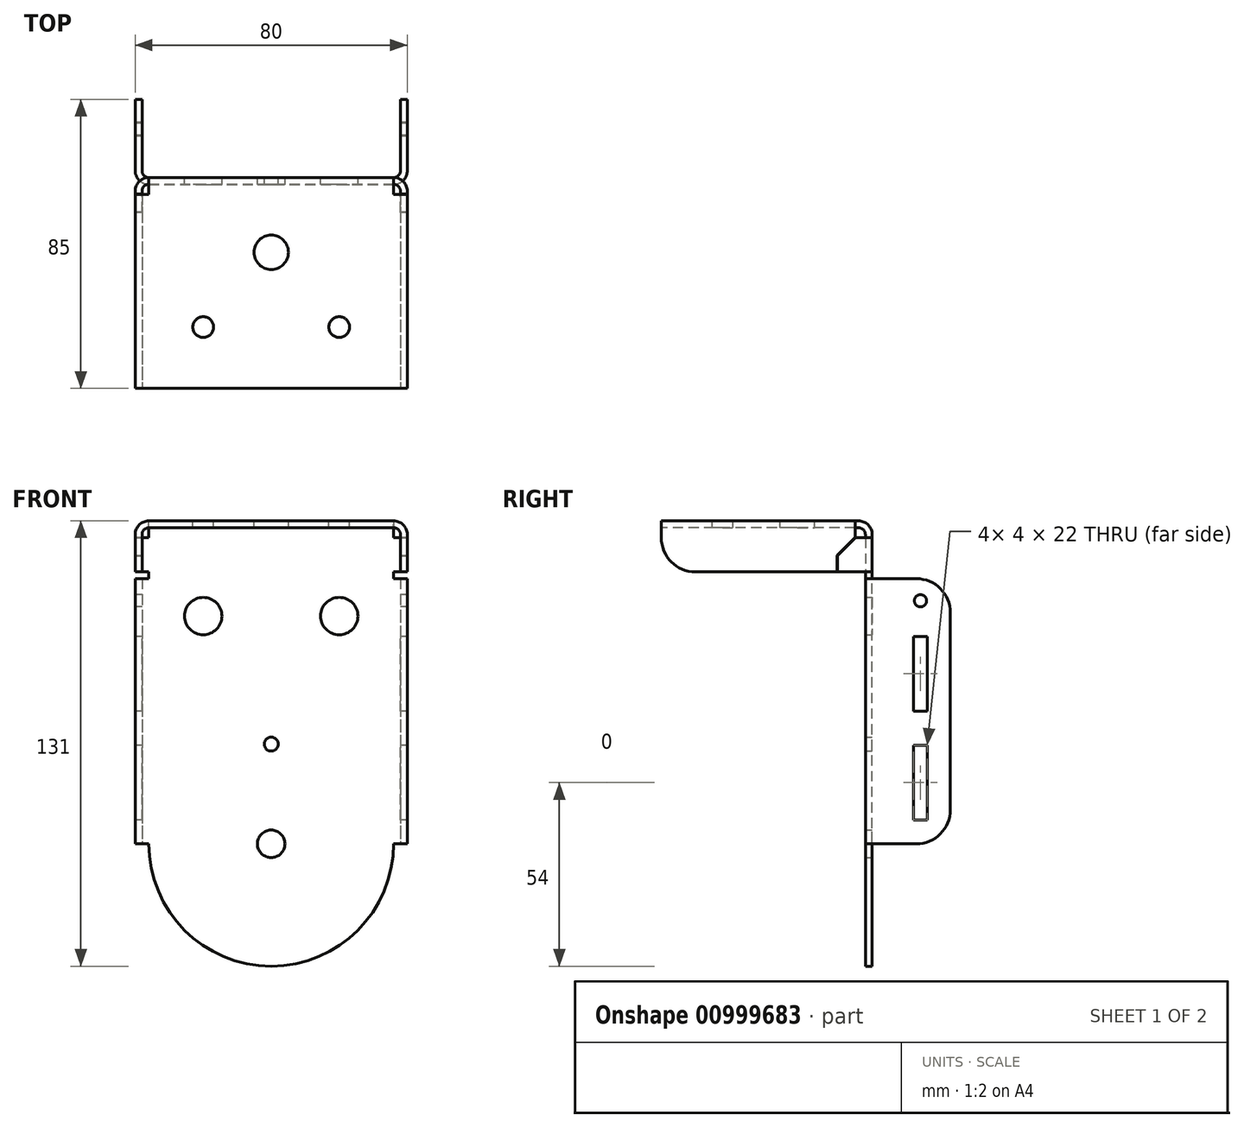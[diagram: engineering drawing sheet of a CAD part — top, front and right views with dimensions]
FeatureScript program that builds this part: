
annotation { "Feature Type Name" : "Feature", "Feature Type Description" : "" }
export const myFeature = defineFeature(function(context is Context, id is Id, definition is map)
    precondition{}
    {
        {
            var Q0;
            Q0=qCreatedBy(makeId("Front.planeOp"),FACE);
            var sketch = newSketch(context, id + "F0", { "sketchPlane" : qUnion([Q0])});
            skCircle(sketch, "E0", {"center": v(0, 0) * mm, "radius": 4.05 * mm});
            skCircle(sketch, "E1", {"center": v(0, 29.34) * mm, "radius": 2.05 * mm});
            skArc(sketch, "E2", {"start": v(-36, 0) * mm, "mid": v(0, -36) * mm, "end": v(36, 0) * mm});
            skLineSegment(sketch, "E3.top", {"start": v(36, 91) * mm, "end": v(-36, 91) * mm});
            skLineSegment(sketch, "E3.left", {"start": v(36, 0) * mm, "end": v(36, 91) * mm});
            skLineSegment(sketch, "E3.right", {"start": v(-36, 0) * mm, "end": v(-36, 91) * mm});
            skSolve(sketch);
        }
        {
            var Q0;
            Q0 = qSketchRegion(id + "F0", true);
            extrude(context, id + "F1", {"entities" : qUnion([Q0]), "depth" : 2 * mm, "offsetDistance" : 25 * mm});
        }
        {
            var Q0;
            Q0=qCreatedBy(makeId("Right.planeOp"),FACE);
            var sketch = newSketch(context, id + "F2", { "sketchPlane" : qUnion([Q0])});
            skArc(sketch, "E4", {"start": v(-2, 91) * mm, "mid": v(-2.59, 92.41) * mm, "end": v(-4, 93) * mm});
            skArc(sketch, "E5", {"start": v(0, 91) * mm, "mid": v(-1.17, 93.83) * mm, "end": v(-4, 95) * mm});
            skLineSegment(sketch, "E6", {"start": v(-2, 91) * mm, "end": v(0, 91) * mm});
            skLineSegment(sketch, "E7", {"start": v(-4, 93) * mm, "end": v(-62, 93) * mm});
            skLineSegment(sketch, "E8", {"start": v(-62, 93) * mm, "end": v(-62, 95) * mm});
            skLineSegment(sketch, "E9", {"start": v(-62, 95) * mm, "end": v(-4, 95) * mm});
            skSolve(sketch);
        }
        {
            var Q0;
            Q0 = qSketchRegion(id + "F2", true);
            extrude(context, id + "F3", {"entities" : qUnion([Q0]), "operationType" : NewBodyOperationType.ADD, "endBound" : BoundingType.SYMMETRIC, "depth" : 72 * mm, "offsetDistance" : 25 * mm});
        }
        {
            var Q0;
            Q0=makeQuery(id+"F3.opExtrude","SWEPT_FACE",FACE,{"disambiguationData":[OSD([sQuery(id+"F2.wireOp",EDGE,"E8")])]});
            var sketch = newSketch(context, id + "F4", { "sketchPlane" : qUnion([Q0])});
            skLineSegment(sketch, "E10", {"start": v(36, 95) * mm, "end": v(36, 93) * mm});
            skArc(sketch, "E11", {"start": v(38, 91) * mm, "mid": v(37.41, 92.41) * mm, "end": v(36, 93) * mm});
            skArc(sketch, "E12", {"start": v(40, 91) * mm, "mid": v(38.83, 93.83) * mm, "end": v(36, 95) * mm});
            skLineSegment(sketch, "E13.top", {"start": v(38, 80) * mm, "end": v(40, 80) * mm});
            skLineSegment(sketch, "E13.left", {"start": v(38, 91) * mm, "end": v(38, 80) * mm});
            skLineSegment(sketch, "E13.right", {"start": v(40, 91) * mm, "end": v(40, 80) * mm});
            skLineSegment(sketch, "E14", {"start": v(-36, 93) * mm, "end": v(-36, 95) * mm});
            skArc(sketch, "E15", {"start": v(-36, 93) * mm, "mid": v(-37.41, 92.41) * mm, "end": v(-38, 91) * mm});
            skArc(sketch, "E16", {"start": v(-36, 95) * mm, "mid": v(-38.83, 93.83) * mm, "end": v(-40, 91) * mm});
            skLineSegment(sketch, "E17.top", {"start": v(-40, 80) * mm, "end": v(-38, 80) * mm});
            skLineSegment(sketch, "E17.left", {"start": v(-40, 91) * mm, "end": v(-40, 80) * mm});
            skLineSegment(sketch, "E17.right", {"start": v(-38, 91) * mm, "end": v(-38, 80) * mm});
            skSolve(sketch);
        }
        {
            var Q0;
            Q0 = qSketchRegion(id + "F4", true);
            extrude(context, id + "F5", {"entities" : qUnion([Q0]), "operationType" : NewBodyOperationType.ADD, "oppositeDirection" : true, "depth" : 58 * mm, "offsetDistance" : 25 * mm});
        }
        {
            var Q0;
            Q0=qCreatedBy(makeId("Top.planeOp"),FACE);
            var sketch = newSketch(context, id + "F6", { "sketchPlane" : qUnion([Q0])});
            skLineSegment(sketch, "E18", {"start": v(-36, -2) * mm, "end": v(-36, 0) * mm});
            skArc(sketch, "E19", {"start": v(-38, 2) * mm, "mid": v(-37.41, 0.59) * mm, "end": v(-36, 0) * mm});
            skArc(sketch, "E20", {"start": v(-40, 2) * mm, "mid": v(-38.83, -0.83) * mm, "end": v(-36, -2) * mm});
            skLineSegment(sketch, "E21.top", {"start": v(-38, 23) * mm, "end": v(-40, 23) * mm});
            skLineSegment(sketch, "E21.left", {"start": v(-38, 2) * mm, "end": v(-38, 23) * mm});
            skLineSegment(sketch, "E21.right", {"start": v(-40, 2) * mm, "end": v(-40, 23) * mm});
            skLineSegment(sketch, "E22", {"start": v(36, 0) * mm, "end": v(36, -2) * mm});
            skArc(sketch, "E23", {"start": v(36, 0) * mm, "mid": v(37.41, 0.59) * mm, "end": v(38, 2) * mm});
            skArc(sketch, "E24", {"start": v(36, -2) * mm, "mid": v(38.83, -0.83) * mm, "end": v(40, 2) * mm});
            skLineSegment(sketch, "E25.top", {"start": v(40, 23) * mm, "end": v(38, 23) * mm});
            skLineSegment(sketch, "E25.left", {"start": v(40, 2) * mm, "end": v(40, 23) * mm});
            skLineSegment(sketch, "E25.right", {"start": v(38, 2) * mm, "end": v(38, 23) * mm});
            skSolve(sketch);
        }
        {
            var Q0;
            Q0 = qSketchRegion(id + "F6", true);
            extrude(context, id + "F7", {"entities" : qUnion([Q0]), "operationType" : NewBodyOperationType.ADD, "depth" : 78 * mm, "offsetDistance" : 25 * mm});
        }
        {
            var Q0;
            Q0=makeQuery(id+"F7.opExtrude","SWEPT_FACE",FACE,{"disambiguationData":[OSD([sQuery(id+"F6.wireOp",EDGE,"E21.right")])]});
            var sketch = newSketch(context, id + "F8", { "sketchPlane" : qUnion([Q0])});
            skLineSegment(sketch, "E26.bottom", {"start": v(-16.21, 7) * mm, "end": v(-12.21, 7) * mm});
            skLineSegment(sketch, "E26.top", {"start": v(-16.21, 61) * mm, "end": v(-12.21, 61) * mm});
            skLineSegment(sketch, "E26.left", {"start": v(-16.21, 7) * mm, "end": v(-16.21, 29) * mm});
            skLineSegment(sketch, "E26.right", {"start": v(-12.21, 7) * mm, "end": v(-12.21, 29) * mm});
            skCircle(sketch, "E27", {"center": v(-14.21, 71.5) * mm, "radius": 1.8 * mm});
            skLineSegment(sketch, "E28", {"start": v(-16.21, 29) * mm, "end": v(-12.21, 29) * mm});
            skLineSegment(sketch, "E29", {"start": v(-16.21, 39) * mm, "end": v(-12.21, 39) * mm});
            skLineSegment(sketch, "E30.trimOffspring", {"start": v(-12.21, 39) * mm, "end": v(-12.21, 61) * mm});
            skLineSegment(sketch, "E31.trimOffspring", {"start": v(-16.21, 39) * mm, "end": v(-16.21, 61) * mm});
            skSolve(sketch);
        }
        {
            var Q0;
            Q0 = qSketchRegion(id + "F8", true);
            extrude(context, id + "F9", {"entities" : qUnion([Q0]), "operationType" : NewBodyOperationType.REMOVE, "endBound" : BoundingType.THROUGH_ALL, "oppositeDirection" : true, "depth" : 25 * mm, "offsetDistance" : 25 * mm});
        }
        {
            var Q0;
            Q0=makeQuery(id+"F7.opExtrude","CAP_EDGE",EDGE,{"disambiguationData":[OSD([sQuery(id+"F6.wireOp",EDGE,"E21.top")])],"isStart":false});
            var Q1;
            Q1=makeQuery(id+"F7.opExtrude","CAP_EDGE",EDGE,{"disambiguationData":[OSD([sQuery(id+"F6.wireOp",EDGE,"E21.top")])],"isStart":true});
            var Q2;
            Q2=makeQuery(id+"F7.opExtrude","CAP_EDGE",EDGE,{"disambiguationData":[OSD([sQuery(id+"F6.wireOp",EDGE,"E25.top")])],"isStart":false});
            var Q3;
            Q3=makeQuery(id+"F7.opExtrude","CAP_EDGE",EDGE,{"disambiguationData":[OSD([sQuery(id+"F6.wireOp",EDGE,"E25.top")])],"isStart":true});
            fillet(context, id + "F10", {"entities" : qUnion([Q0, Q1, Q2, Q3]), "radius" : 10 * mm, "tangentPropagation" : true, "allowEdgeOverflow" : false});
        }
        {
            var Q0;
            Q0=makeQuery(id+"F5.opExtrude","CAP_EDGE",EDGE,{"disambiguationData":[OSD([sQuery(id+"F4.wireOp",EDGE,"E13.top")])],"isStart":true});
            var Q1;
            Q1=makeQuery(id+"F5.opExtrude","CAP_EDGE",EDGE,{"disambiguationData":[OSD([sQuery(id+"F4.wireOp",EDGE,"E17.top")])],"isStart":true});
            fillet(context, id + "F11", {"entities" : qUnion([Q0, Q1]), "radius" : 10 * mm, "tangentPropagation" : true, "allowEdgeOverflow" : false});
        }
        {
            var Q0;
            Q0=makeQuery(id+"F5.opExtrude","SWEPT_FACE",FACE,{"disambiguationData":[OSD([sQuery(id+"F4.wireOp",EDGE,"E13.top")])]});
            var sketch = newSketch(context, id + "F12", { "sketchPlane" : qUnion([Q0])});
            skLineSegment(sketch, "E32", {"start": v(-36, 2) * mm, "end": v(-36, 0) * mm});
            skArc(sketch, "E33", {"start": v(-38, 4) * mm, "mid": v(-37.41, 2.58) * mm, "end": v(-36, 2) * mm});
            skArc(sketch, "E34", {"start": v(-40, 4) * mm, "mid": v(-38.83, 1.17) * mm, "end": v(-36, 0) * mm});
            skLineSegment(sketch, "E35", {"start": v(-38, 4) * mm, "end": v(-40, 4) * mm});
            skLineSegment(sketch, "E36", {"start": v(36, 2) * mm, "end": v(36, 0) * mm});
            skArc(sketch, "E37", {"start": v(36, 2) * mm, "mid": v(37.41, 2.59) * mm, "end": v(38, 4) * mm});
            skArc(sketch, "E38", {"start": v(36, 0) * mm, "mid": v(38.83, 1.17) * mm, "end": v(40, 4) * mm});
            skLineSegment(sketch, "E39", {"start": v(38, 4) * mm, "end": v(40, 4) * mm});
            skSolve(sketch);
        }
        {
            var Q0;
            Q0 = qSketchRegion(id + "F12", true);
            extrude(context, id + "F13", {"entities" : qUnion([Q0]), "operationType" : NewBodyOperationType.ADD, "oppositeDirection" : true, "depth" : 11 * mm, "offsetDistance" : 25 * mm});
        }
        {
            var Q0;
            Q0=makeQuery(id+"F1.opExtrude","CAP_FACE",FACE,{"disambiguationData":[OSD([sQuery(id+"F0.wireOp",EDGE,"E0"),sQuery(id+"F0.wireOp",EDGE,"E1"),sQuery(id+"F0.wireOp",EDGE,"E2"),sQuery(id+"F0.wireOp",EDGE,"E3.top"),sQuery(id+"F0.wireOp",EDGE,"E3.left"),sQuery(id+"F0.wireOp",EDGE,"E3.right")])],"isStart":true});
            var sketch = newSketch(context, id + "F14", { "sketchPlane" : qUnion([Q0])});
            skLineSegment(sketch, "E40.bottom", {"start": v(36, 90) * mm, "end": v(47.67, 90) * mm});
            skLineSegment(sketch, "E40.top", {"start": v(36, 97.26) * mm, "end": v(47.67, 97.26) * mm});
            skLineSegment(sketch, "E40.left", {"start": v(36, 90) * mm, "end": v(36, 97.26) * mm});
            skLineSegment(sketch, "E40.right", {"start": v(47.67, 90) * mm, "end": v(47.67, 97.26) * mm});
            skLineSegment(sketch, "E41.bottom", {"start": v(-36, 90) * mm, "end": v(-46.95, 90) * mm});
            skLineSegment(sketch, "E41.top", {"start": v(-36, 97.57) * mm, "end": v(-46.95, 97.57) * mm});
            skLineSegment(sketch, "E41.left", {"start": v(-36, 90) * mm, "end": v(-36, 97.57) * mm});
            skLineSegment(sketch, "E41.right", {"start": v(-46.95, 90) * mm, "end": v(-46.95, 97.57) * mm});
            skSolve(sketch);
        }
        {
            var Q0;
            Q0 = qSketchRegion(id + "F14", true);
            extrude(context, id + "F15", {"entities" : qUnion([Q0]), "operationType" : NewBodyOperationType.REMOVE, "oppositeDirection" : true, "depth" : 5 * mm, "offsetDistance" : 25 * mm});
        }
        {
            var Q0;
            Q0=makeQuery(id+"F5.opExtrude","SWEPT_FACE",FACE,{"disambiguationData":[OSD([sQuery(id+"F4.wireOp",EDGE,"E13.right")])]});
            var sketch = newSketch(context, id + "F16", { "sketchPlane" : qUnion([Q0])});
            skLineSegment(sketch, "E42", {"start": v(-4.07, 91.07) * mm, "end": v(-10.35, 84.8) * mm});
            skLineSegment(sketch, "E43", {"start": v(-4.2, 90.66) * mm, "end": v(-10.15, 84.71) * mm});
            skLineSegment(sketch, "E44", {"start": v(-4.2, 90.66) * mm, "end": v(-4.07, 91.07) * mm});
            skLineSegment(sketch, "E45.top", {"start": v(-10.35, 79.14) * mm, "end": v(-10.15, 79.14) * mm});
            skLineSegment(sketch, "E45.left", {"start": v(-10.35, 84.8) * mm, "end": v(-10.35, 79.14) * mm});
            skLineSegment(sketch, "E45.right", {"start": v(-10.15, 84.71) * mm, "end": v(-10.15, 79.14) * mm});
            skPoint(sketch, "E46.end.orphan", {"position": v(-16.62, 78.52) * mm});
            skSolve(sketch);
        }
        {
            var Q0;
            Q0 = qSketchRegion(id + "F16", true);
            extrude(context, id + "F17", {"entities" : qUnion([Q0]), "operationType" : NewBodyOperationType.REMOVE, "oppositeDirection" : true, "depth" : 100 * mm, "offsetDistance" : 25 * mm});
        }
        {
            var Q0;
            Q0=makeQuery(id+"F3.opExtrude","SWEPT_FACE",FACE,{"disambiguationData":[OSD([sQuery(id+"F2.wireOp",EDGE,"E9")])]});
            var sketch = newSketch(context, id + "F18", { "sketchPlane" : qUnion([Q0])});
            skCircle(sketch, "E47", {"center": v(0, -22) * mm, "radius": 5.05 * mm});
            skCircle(sketch, "E48", {"center": v(20, -44) * mm, "radius": 3.05 * mm});
            skCircle(sketch, "E49", {"center": v(-20, -44) * mm, "radius": 3.05 * mm});
            skSolve(sketch);
        }
        {
            var Q0;
            Q0 = qSketchRegion(id + "F18", true);
            extrude(context, id + "F19", {"entities" : qUnion([Q0]), "operationType" : NewBodyOperationType.REMOVE, "oppositeDirection" : true, "depth" : 25 * mm, "offsetDistance" : 25 * mm});
        }
        {
            var Q0;
            Q0=makeQuery(id+"F1.opExtrude","CAP_FACE",FACE,{"disambiguationData":[OSD([sQuery(id+"F0.wireOp",EDGE,"E0"),sQuery(id+"F0.wireOp",EDGE,"E1"),sQuery(id+"F0.wireOp",EDGE,"E2"),sQuery(id+"F0.wireOp",EDGE,"E3.top"),sQuery(id+"F0.wireOp",EDGE,"E3.left"),sQuery(id+"F0.wireOp",EDGE,"E3.right")])],"isStart":true});
            var sketch = newSketch(context, id + "F20", { "sketchPlane" : qUnion([Q0])});
            skCircle(sketch, "E50", {"center": v(-20, 67) * mm, "radius": 5.5 * mm});
            skCircle(sketch, "E51", {"center": v(20, 67) * mm, "radius": 5.5 * mm});
            skSolve(sketch);
        }
        {
            var Q0;
            Q0 = qSketchRegion(id + "F20", true);
            extrude(context, id + "F21", {"entities" : qUnion([Q0]), "operationType" : NewBodyOperationType.REMOVE, "oppositeDirection" : true, "depth" : 25 * mm, "offsetDistance" : 25 * mm});
        }
    });
